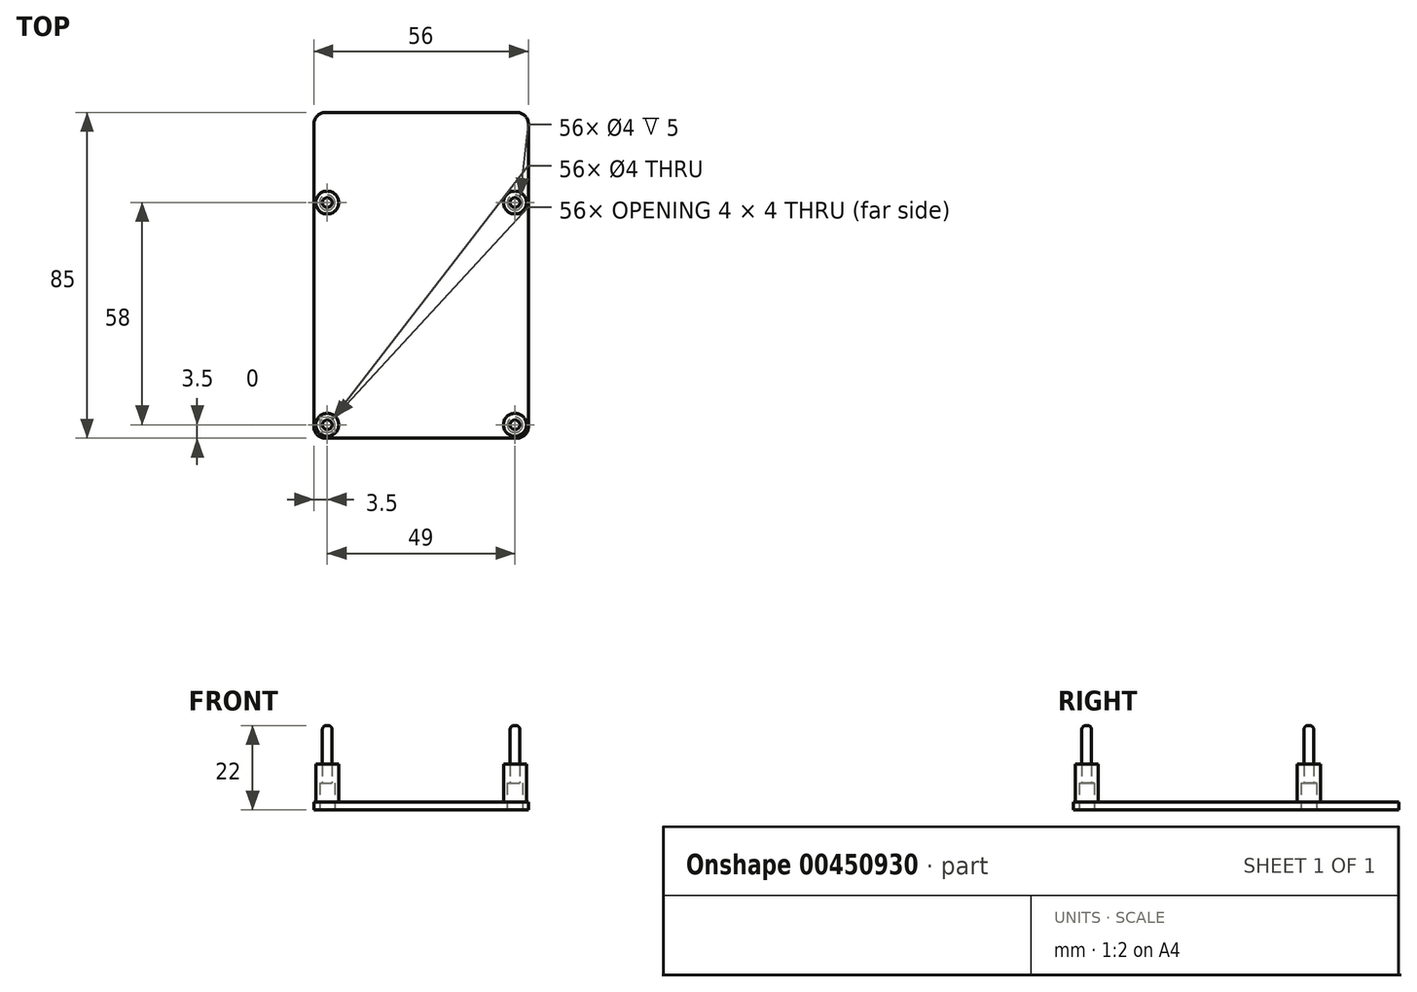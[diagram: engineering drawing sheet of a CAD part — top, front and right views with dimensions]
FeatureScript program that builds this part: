
annotation { "Feature Type Name" : "Feature", "Feature Type Description" : "" }
export const myFeature = defineFeature(function(context is Context, id is Id, definition is map)
    precondition{}
    {
        {
            var Q0;
            Q0=qCreatedBy(makeId("Top.planeOp"),FACE);
            var sketch = newSketch(context, id + "F0", { "sketchPlane" : qUnion([Q0])});
            skLineSegment(sketch, "E0.bottom", {"start": v(28, -42.5) * mm, "end": v(-28, -42.5) * mm});
            skLineSegment(sketch, "E0.top", {"start": v(28, 42.5) * mm, "end": v(-28, 42.5) * mm});
            skLineSegment(sketch, "E0.left", {"start": v(28, -42.5) * mm, "end": v(28, 42.5) * mm});
            skLineSegment(sketch, "E0.right", {"start": v(-28, -42.5) * mm, "end": v(-28, 42.5) * mm});
            skPoint(sketch, "E0.middle", {"position": v(0, 0) * mm});
            skSolve(sketch);
        }
        {
            var Q0;
            Q0 = qSketchRegion(id + "F0", true);
            extrude(context, id + "F1", {"entities" : qUnion([Q0]), "depth" : 2 * mm, "offsetDistance" : 25 * mm});
        }
        {
            var Q0;
            Q0=makeQuery(id+"F1.opExtrude","SWEPT_EDGE",EDGE,{"disambiguationData":[OSD([sQuery(id+"F0.wireOp",EDGE,"E0.top"),sQuery(id+"F0.wireOp",EDGE,"E0.right")])]});
            var Q1;
            Q1=makeQuery(id+"F1.opExtrude","SWEPT_EDGE",EDGE,{"disambiguationData":[OSD([sQuery(id+"F0.wireOp",EDGE,"E0.top"),sQuery(id+"F0.wireOp",EDGE,"E0.left")])]});
            var Q2;
            Q2=makeQuery(id+"F1.opExtrude","SWEPT_EDGE",EDGE,{"disambiguationData":[OSD([sQuery(id+"F0.wireOp",EDGE,"E0.bottom"),sQuery(id+"F0.wireOp",EDGE,"E0.left")])]});
            var Q3;
            Q3=makeQuery(id+"F1.opExtrude","SWEPT_EDGE",EDGE,{"disambiguationData":[OSD([sQuery(id+"F0.wireOp",EDGE,"E0.bottom"),sQuery(id+"F0.wireOp",EDGE,"E0.right")])]});
            fillet(context, id + "F2", {"entities" : qUnion([Q0, Q1, Q2, Q3]), "radius" : 3 * mm, "tangentPropagation" : true, "allowEdgeOverflow" : false});
        }
        {
            var Q0;
            Q0=makeQuery(id+"F1.opExtrude","CAP_FACE",FACE,{"disambiguationData":[OSD([sQuery(id+"F0.wireOp",EDGE,"E0.bottom"),sQuery(id+"F0.wireOp",EDGE,"E0.top"),sQuery(id+"F0.wireOp",EDGE,"E0.left"),sQuery(id+"F0.wireOp",EDGE,"E0.right")])],"isStart":false});
            var sketch = newSketch(context, id + "F3", { "sketchPlane" : qUnion([Q0])});
            skCircle(sketch, "E1", {"center": v(-24.5, -39) * mm, "radius": 1.25 * mm});
            skCircle(sketch, "E2", {"center": v(24.5, -39) * mm, "radius": 1.25 * mm});
            skCircle(sketch, "E3", {"center": v(-24.5, 19) * mm, "radius": 1.25 * mm});
            skCircle(sketch, "E4", {"center": v(24.5, 19) * mm, "radius": 1.25 * mm});
            skSolve(sketch);
        }
        {
            var Q0;
            Q0=makeQuery(id+"F3.imprint","IMPRINT",FACE,{"disambiguationData":[TD([[makeQuery(id+"F3.imprint","IMPRINT",EDGE,{"derivedFrom":sQuery(id+"F3.wireOp",EDGE,"E1")}),-1.0]])]});
            var sketch = newSketch(context, id + "F4", { "sketchPlane" : qUnion([Q0])});
            skCircle(sketch, "E5", {"center": v(-24.5, 19) * mm, "radius": 3 * mm});
            skCircle(sketch, "E6", {"center": v(24.5, 19) * mm, "radius": 3 * mm});
            skCircle(sketch, "E7", {"center": v(-24.5, -39) * mm, "radius": 3 * mm});
            skCircle(sketch, "E8", {"center": v(24.5, -39) * mm, "radius": 3 * mm});
            skSolve(sketch);
        }
        {
            var Q0;
            Q0 = qSketchRegion(id + "F3", true);
            extrude(context, id + "F5", {"entities" : qUnion([Q0]), "depth" : 20 * mm, "offsetDistance" : 25 * mm});
        }
        {
            var Q0;
            Q0 = qSketchRegion(id + "F4", true);
            extrude(context, id + "F6", {"entities" : qUnion([Q0]), "depth" : 10 * mm, "offsetDistance" : 25 * mm});
        }
        {
            var Q0;
            Q0=makeQuery(id+"F1.opExtrude","CAP_FACE",FACE,{"disambiguationData":[OSD([sQuery(id+"F0.wireOp",EDGE,"E0.bottom"),sQuery(id+"F0.wireOp",EDGE,"E0.top"),sQuery(id+"F0.wireOp",EDGE,"E0.left"),sQuery(id+"F0.wireOp",EDGE,"E0.right")])],"isStart":true});
            var sketch = newSketch(context, id + "F7", { "sketchPlane" : qUnion([Q0])});
            skCircle(sketch, "E9", {"center": v(-24.5, 39) * mm, "radius": 2 * mm});
            skCircle(sketch, "E10", {"center": v(24.5, 39) * mm, "radius": 2 * mm});
            skCircle(sketch, "E11", {"center": v(-24.5, -19) * mm, "radius": 2 * mm});
            skCircle(sketch, "E12", {"center": v(24.5, -19) * mm, "radius": 2 * mm});
            skSolve(sketch);
        }
        {
            var Q0;
            Q0 = qSketchRegion(id + "F7", true);
            extrude(context, id + "F8", {"entities" : qUnion([Q0]), "operationType" : NewBodyOperationType.REMOVE, "oppositeDirection" : true, "depth" : 7 * mm, "offsetDistance" : 25 * mm});
        }
        {
            var Q0;
            Q0=makeQuery(id+"F5.opExtrude","CAP_EDGE",EDGE,{"disambiguationData":[OSD([sQuery(id+"F3.wireOp",EDGE,"E3")])],"isStart":false});
            var Q1;
            Q1=makeQuery(id+"F5.opExtrude","CAP_EDGE",EDGE,{"disambiguationData":[OSD([sQuery(id+"F3.wireOp",EDGE,"E1")])],"isStart":false});
            var Q2;
            Q2=makeQuery(id+"F5.opExtrude","CAP_EDGE",EDGE,{"disambiguationData":[OSD([sQuery(id+"F3.wireOp",EDGE,"E2")])],"isStart":false});
            var Q3;
            Q3=makeQuery(id+"F5.opExtrude","CAP_EDGE",EDGE,{"disambiguationData":[OSD([sQuery(id+"F3.wireOp",EDGE,"E4")])],"isStart":false});
            fillet(context, id + "F9", {"entities" : qUnion([Q0, Q1, Q2, Q3]), "radius" : 1 * mm, "tangentPropagation" : true, "allowEdgeOverflow" : false});
        }
    });
